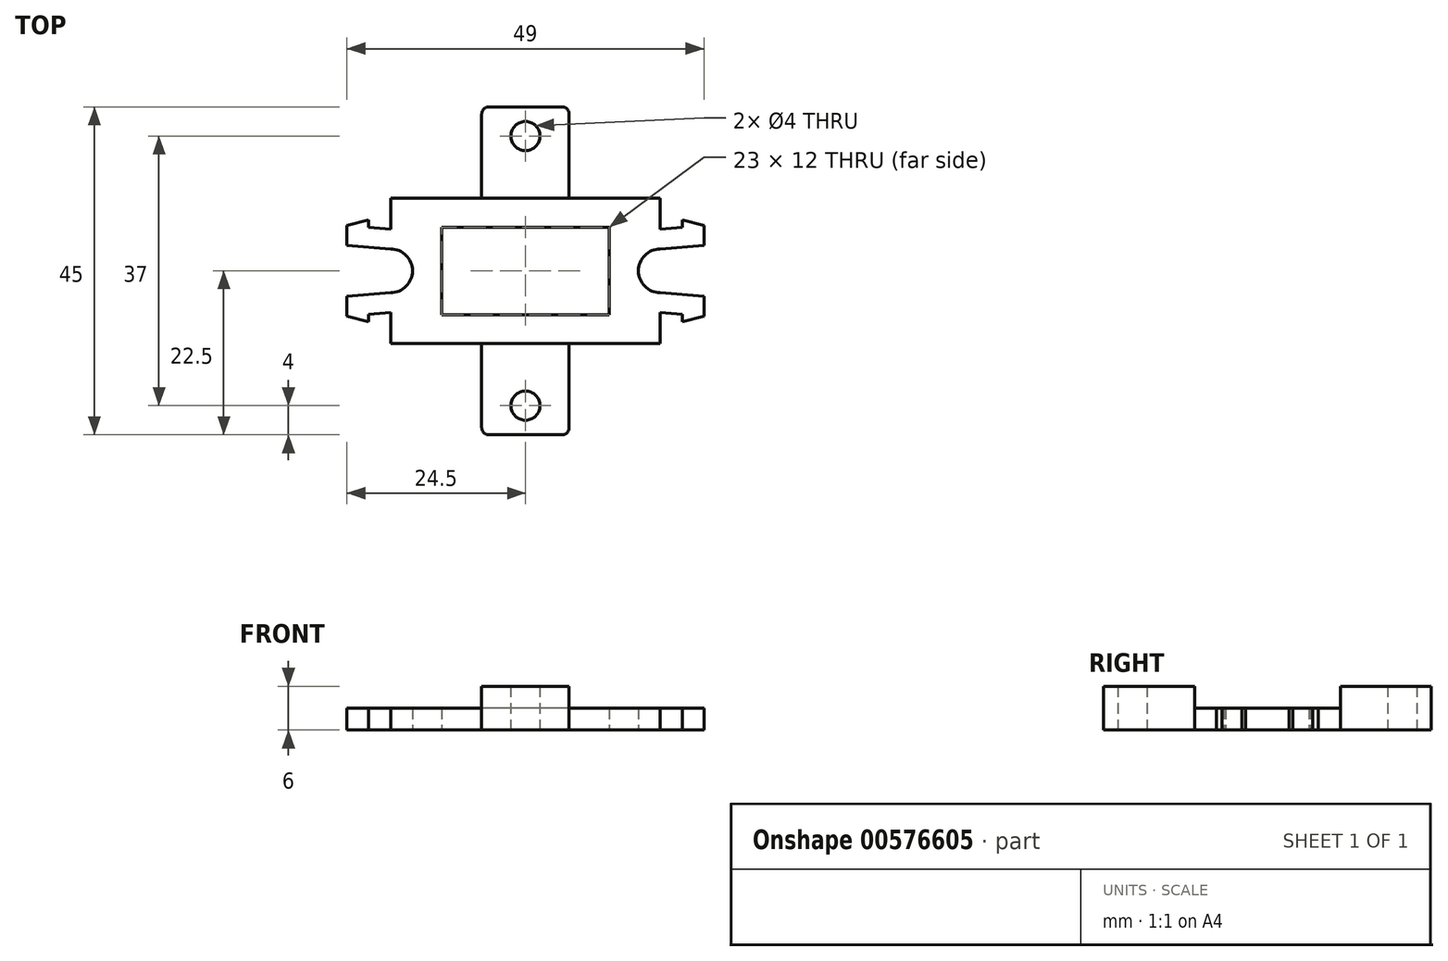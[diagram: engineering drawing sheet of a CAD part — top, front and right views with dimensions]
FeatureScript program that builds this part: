
annotation { "Feature Type Name" : "Feature", "Feature Type Description" : "" }
export const myFeature = defineFeature(function(context is Context, id is Id, definition is map)
    precondition{}
    {
        {
            var Q0;
            Q0=qCreatedBy(makeId("Top.planeOp"),FACE);
            var sketch = newSketch(context, id + "F0", { "sketchPlane" : qUnion([Q0])});
            skLineSegment(sketch, "E0.rect.bottom", {"start": v(18.5, 10) * mm, "end": v(-18.5, 10) * mm});
            skLineSegment(sketch, "E0.rect.top", {"start": v(18.5, -10) * mm, "end": v(-18.5, -10) * mm});
            skLineSegment(sketch, "E0.rect.left", {"start": v(18.5, 10) * mm, "end": v(18.5, 7) * mm});
            skLineSegment(sketch, "E0.rect.right", {"start": v(-18.5, 10) * mm, "end": v(-18.5, 7) * mm});
            skPoint(sketch, "E0.rect.middle", {"position": v(0, 0) * mm});
            skLineSegment(sketch, "E1.rect.bottom", {"start": v(24.5, 7) * mm, "end": v(18.5, 7) * mm, "construction": true});
            skLineSegment(sketch, "E1.rect.top", {"start": v(24.5, -7) * mm, "end": v(18.5, -7) * mm, "construction": true});
            skLineSegment(sketch, "E1.rect.left", {"start": v(24.5, 3.5) * mm, "end": v(24.5, -3.5) * mm, "construction": true});
            skLineSegment(sketch, "E1.rect.right", {"start": v(-24.5, 7) * mm, "end": v(-24.5, -7) * mm, "construction": true});
            skLineSegment(sketch, "E2.trimOffspring", {"start": v(-18.5, 7) * mm, "end": v(-24.5, 7) * mm, "construction": true});
            skLineSegment(sketch, "E3.trimOffspring", {"start": v(-18.5, -7) * mm, "end": v(-18.5, -10) * mm});
            skLineSegment(sketch, "E4.trimOffspring", {"start": v(-18.5, -7) * mm, "end": v(-24.5, -7) * mm, "construction": true});
            skLineSegment(sketch, "E5.trimOffspring", {"start": v(18.5, -7) * mm, "end": v(18.5, -10) * mm});
            skLineSegment(sketch, "E6", {"start": v(-18.5, 3) * mm, "end": v(-18.5, -5.7) * mm, "construction": true});
            skLineSegment(sketch, "E7", {"start": v(18.5, 7) * mm, "end": v(18.5, 5.7) * mm, "construction": true});
            skArc(sketch, "E8", {"start": v(-18.5, -3) * mm, "mid": v(-15.5, 0) * mm, "end": v(-18.5, 3) * mm});
            skArc(sketch, "E9", {"start": v(18.5, 3) * mm, "mid": v(15.5, 0) * mm, "end": v(18.5, -3) * mm});
            skLineSegment(sketch, "E10", {"start": v(-18.5, 3) * mm, "end": v(-24.5, 3.5) * mm});
            skLineSegment(sketch, "E11", {"start": v(-18.5, -3) * mm, "end": v(-24.5, -3.5) * mm});
            skLineSegment(sketch, "E12", {"start": v(-24.5, 7) * mm, "end": v(-24.5, 3.5) * mm, "construction": true});
            skLineSegment(sketch, "E13", {"start": v(-24.5, -3.5) * mm, "end": v(-24.5, -7) * mm, "construction": true});
            skLineSegment(sketch, "E14", {"start": v(-24.5, 6.2) * mm, "end": v(-18.5, 5.7) * mm, "construction": true});
            skLineSegment(sketch, "E15", {"start": v(-18.5, 5.7) * mm, "end": v(-18.5, 3) * mm, "construction": true});
            skLineSegment(sketch, "E16", {"start": v(-21.5, 3.25) * mm, "end": v(-21.5, 5.95) * mm, "construction": true});
            skLineSegment(sketch, "E17", {"start": v(-18.5, 7) * mm, "end": v(-18.5, 5.7) * mm, "construction": true});
            skLineSegment(sketch, "E18", {"start": v(-18.5, 5.7) * mm, "end": v(-21.5, 5.95) * mm});
            skLineSegment(sketch, "E19", {"start": v(-24.5, 6.2) * mm, "end": v(-24.5, 3.5) * mm});
            skLineSegment(sketch, "E20", {"start": v(-18.5, 5.7) * mm, "end": v(-18.5, 7) * mm});
            skLineSegment(sketch, "E21", {"start": v(-24.5, -6.2) * mm, "end": v(-18.5, -5.7) * mm, "construction": true});
            skLineSegment(sketch, "E22", {"start": v(-18.5, -3) * mm, "end": v(-18.5, -5.7) * mm, "construction": true});
            skLineSegment(sketch, "E23", {"start": v(-18.5, -5.7) * mm, "end": v(-18.5, -7) * mm});
            skLineSegment(sketch, "E24", {"start": v(-18.5, -5.7) * mm, "end": v(-21.5, -5.95) * mm});
            skLineSegment(sketch, "E25", {"start": v(-24.5, -3.5) * mm, "end": v(-24.5, -6.2) * mm});
            skLineSegment(sketch, "E26", {"start": v(-24.5, 6.2) * mm, "end": v(-21.5, 7) * mm});
            skLineSegment(sketch, "E27", {"start": v(-21.5, 7) * mm, "end": v(-21.5, 5.95) * mm});
            skLineSegment(sketch, "E28", {"start": v(-24.5, -6.2) * mm, "end": v(-21.5, -7) * mm});
            skLineSegment(sketch, "E29", {"start": v(-21.5, -7) * mm, "end": v(-21.5, -5.95) * mm});
            skLineSegment(sketch, "E30", {"start": v(18.5, 3) * mm, "end": v(24.5, 3.5) * mm});
            skLineSegment(sketch, "E31", {"start": v(18.5, -3) * mm, "end": v(24.5, -3.5) * mm});
            skLineSegment(sketch, "E32", {"start": v(24.5, 7) * mm, "end": v(24.5, 3.5) * mm, "construction": true});
            skLineSegment(sketch, "E33", {"start": v(24.5, -3.5) * mm, "end": v(24.5, -7) * mm, "construction": true});
            skLineSegment(sketch, "E34", {"start": v(24.5, 6.2) * mm, "end": v(18.5, 5.7) * mm, "construction": true});
            skLineSegment(sketch, "E35", {"start": v(18.5, -5.7) * mm, "end": v(24.5, -6.2) * mm, "construction": true});
            skLineSegment(sketch, "E36.trimOffspring", {"start": v(18.5, 3) * mm, "end": v(18.5, -3) * mm, "construction": true});
            skLineSegment(sketch, "E37.trimOffspring", {"start": v(18.5, -5.7) * mm, "end": v(18.5, -7) * mm, "construction": true});
            skLineSegment(sketch, "E38", {"start": v(18.5, 5.7) * mm, "end": v(18.5, 3) * mm, "construction": true});
            skLineSegment(sketch, "E39", {"start": v(18.5, -3) * mm, "end": v(18.5, -5.7) * mm, "construction": true});
            skLineSegment(sketch, "E40", {"start": v(24.5, 3.5) * mm, "end": v(24.5, 6.2) * mm});
            skLineSegment(sketch, "E41", {"start": v(24.5, 6.2) * mm, "end": v(21.5, 7) * mm});
            skLineSegment(sketch, "E42", {"start": v(21.5, 7) * mm, "end": v(21.5, 5.95) * mm});
            skLineSegment(sketch, "E43", {"start": v(21.5, 5.95) * mm, "end": v(18.5, 5.7) * mm});
            skLineSegment(sketch, "E44", {"start": v(24.5, -3.5) * mm, "end": v(24.5, -6.2) * mm});
            skLineSegment(sketch, "E45", {"start": v(24.5, -6.2) * mm, "end": v(21.5, -7) * mm});
            skLineSegment(sketch, "E46", {"start": v(21.5, -7) * mm, "end": v(21.5, -5.95) * mm});
            skLineSegment(sketch, "E47", {"start": v(21.5, -5.95) * mm, "end": v(18.5, -5.7) * mm});
            skLineSegment(sketch, "E48", {"start": v(18.5, 5.7) * mm, "end": v(18.5, 7) * mm});
            skLineSegment(sketch, "E49", {"start": v(18.5, -5.7) * mm, "end": v(18.5, -7) * mm});
            skLineSegment(sketch, "E50.rect.bottom", {"start": v(11.5, 6) * mm, "end": v(-11.5, 6) * mm});
            skLineSegment(sketch, "E50.rect.top", {"start": v(11.5, -6) * mm, "end": v(-11.5, -6) * mm});
            skLineSegment(sketch, "E50.rect.left", {"start": v(11.5, 6) * mm, "end": v(11.5, -6) * mm});
            skLineSegment(sketch, "E50.rect.right", {"start": v(-11.5, 6) * mm, "end": v(-11.5, -6) * mm});
            skSolve(sketch);
        }
        {
            var Q0;
            Q0=makeQuery(id+"F0.imprint","IMPRINT",FACE,{"disambiguationData":[TD([[makeQuery(id+"F0.imprint","IMPRINT",EDGE,{"derivedFrom":sQuery(id+"F0.wireOp",EDGE,"E0.rect.bottom")}),1.0]])]});
            extrude(context, id + "F1", {"entities" : qUnion([Q0]), "depth" : 3 * mm});
        }
        {
            var Q0;
            Q0=qCreatedBy(makeId("Top.planeOp"),FACE);
            var sketch = newSketch(context, id + "F2", { "sketchPlane" : qUnion([Q0])});
            skLineSegment(sketch, "E51.rect.bottom", {"start": v(6, 22.5) * mm, "end": v(-6, 22.5) * mm, "construction": true});
            skLineSegment(sketch, "E51.rect.top", {"start": v(6, -22.5) * mm, "end": v(-6, -22.5) * mm, "construction": true});
            skLineSegment(sketch, "E51.rect.left", {"start": v(6, 22.5) * mm, "end": v(6, -22.5) * mm, "construction": true});
            skLineSegment(sketch, "E51.rect.right", {"start": v(-6, 22.5) * mm, "end": v(-6, -22.5) * mm, "construction": true});
            skPoint(sketch, "E51.rect.middle", {"position": v(0, 0) * mm});
            skLineSegment(sketch, "E52", {"start": v(0, -18.5) * mm, "end": v(0, 18.5) * mm, "construction": true});
            skCircle(sketch, "E53", {"center": v(0, 18.5) * mm, "radius": 2 * mm});
            skCircle(sketch, "E54", {"center": v(0, -18.5) * mm, "radius": 2 * mm});
            skLineSegment(sketch, "E55.0", {"start": v(6, 10) * mm, "end": v(-6, 10) * mm});
            skLineSegment(sketch, "E56", {"start": v(6, 10) * mm, "end": v(6, 21.5) * mm});
            skLineSegment(sketch, "E57", {"start": v(-6, 21.5) * mm, "end": v(-6, 10) * mm});
            skLineSegment(sketch, "E58", {"start": v(-5, 22.5) * mm, "end": v(5, 22.5) * mm});
            skLineSegment(sketch, "E59.0", {"start": v(6, -10) * mm, "end": v(-6, -10) * mm});
            skLineSegment(sketch, "E60", {"start": v(-6, -10) * mm, "end": v(-6, -21.5) * mm});
            skLineSegment(sketch, "E61", {"start": v(-5, -22.5) * mm, "end": v(5, -22.5) * mm});
            skLineSegment(sketch, "E62", {"start": v(6, -21.5) * mm, "end": v(6, -10) * mm});
            skPoint(sketch, "E63.visualSharp", {"position": v(-6, 22.5) * mm});
            skArc(sketch, "E63.filletArc", {"start": v(-5, 22.5) * mm, "mid": v(-5.7, 22.2) * mm, "end": v(-6, 21.5) * mm});
            skPoint(sketch, "E64.visualSharp", {"position": v(6, 22.5) * mm});
            skArc(sketch, "E64.filletArc", {"start": v(6, 21.5) * mm, "mid": v(5.7, 22.2) * mm, "end": v(5, 22.5) * mm});
            skPoint(sketch, "E65.visualSharp", {"position": v(6, -22.5) * mm});
            skArc(sketch, "E65.filletArc", {"start": v(5, -22.5) * mm, "mid": v(5.7, -22.2) * mm, "end": v(6, -21.5) * mm});
            skPoint(sketch, "E66.visualSharp", {"position": v(-6, -22.5) * mm});
            skArc(sketch, "E66.filletArc", {"start": v(-6, -21.5) * mm, "mid": v(-5.7, -22.2) * mm, "end": v(-5, -22.5) * mm});
            skSolve(sketch);
        }
        {
            var Q0;
            Q0=makeQuery(id+"F2.imprint","IMPRINT",FACE,{"disambiguationData":[TD([[makeQuery(id+"F2.imprint","IMPRINT",EDGE,{"derivedFrom":sQuery(id+"F2.wireOp",EDGE,"E53")}),-1.0]])]});
            var Q1;
            Q1=makeQuery(id+"F2.imprint","IMPRINT",FACE,{"disambiguationData":[TD([[makeQuery(id+"F2.imprint","IMPRINT",EDGE,{"derivedFrom":sQuery(id+"F2.wireOp",EDGE,"E54")}),-1.0]])]});
            extrude(context, id + "F3", {"entities" : qUnion([Q0, Q1]), "operationType" : NewBodyOperationType.ADD, "depth" : 6 * mm});
        }
    });
